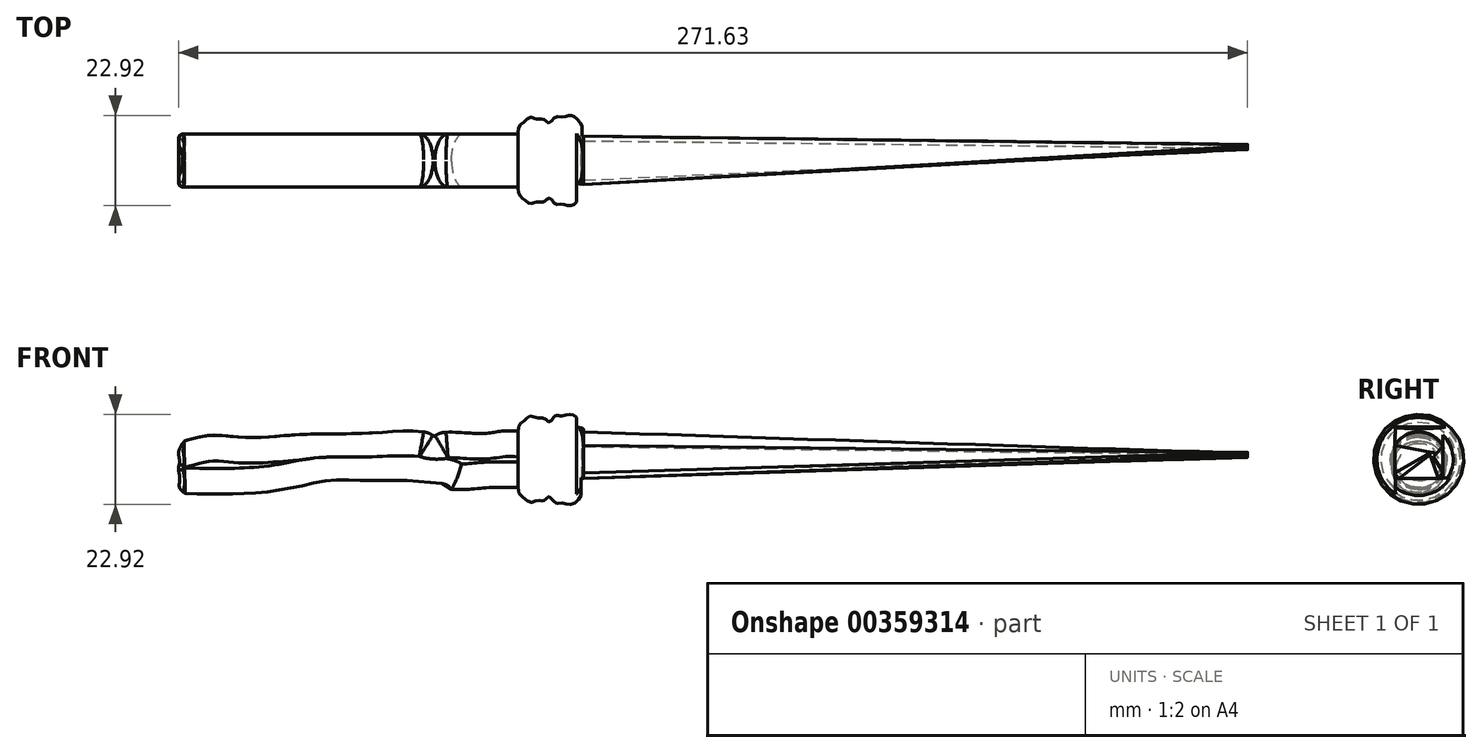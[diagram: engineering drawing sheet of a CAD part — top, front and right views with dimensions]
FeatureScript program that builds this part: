
annotation { "Feature Type Name" : "Feature", "Feature Type Description" : "" }
export const myFeature = defineFeature(function(context is Context, id is Id, definition is map)
    precondition{}
    {
        {
            var Q0;
            Q0=qCreatedBy(makeId("Front.planeOp"),FACE);
            var sketch = newSketch(context, id + "F0", { "sketchPlane" : qUnion([Q0])});
            skFitSpline(sketch, "E0", {"points": [v(-136.71, 3.5) * mm, v(-129.4, 4.98) * mm, v(-121.58, 4.4) * mm, v(-107.37, 5.13) * mm, v(-92.29, 5.42) * mm, v(-84.6, 5.85) * mm, v(-74.74, 5.56) * mm, v(-73.15, 4.84) * mm, v(-71.4, 5.56) * mm, v(-61.4, 5.42) * mm, v(-56.04, 6) * mm, v(-51.83, 6) * mm], "startDerivative": vector(88.1, 22.8) * mm, "endDerivative": vector(61.32, -2.92) * mm});
            skFitSpline(sketch, "E1", {"points": [v(-136.42, -9.83) * mm, v(-121.1, -9.83) * mm, v(-111.3, -8.78) * mm, v(-105.26, -7.5) * mm, v(-100.26, -6.52) * mm, v(-91.17, -6.52) * mm, v(-80.75, -6.52) * mm, v(-73.68, -7) * mm, v(-69.65, -7.8) * mm, v(-68.74, -8.78) * mm], "startDerivative": vector(97.79, -2) * mm, "endDerivative": vector(13.86, -22.1) * mm});
            skFitSpline(sketch, "E2", {"points": [v(-68.74, -8.78) * mm, v(-64.65, -8.78) * mm, v(-58.92, -8.29) * mm, v(-54.41, -8.29) * mm, v(-51.73, -8.29) * mm], "startDerivative": vector(15.61, -0.53) * mm, "endDerivative": vector(12, 0.12) * mm});
            skLineSegment(sketch, "E3", {"start": v(-51.83, 6) * mm, "end": v(-51.83, -8.29) * mm});
            skLineSegment(sketch, "E4", {"start": v(-136.71, 3.5) * mm, "end": v(-136.42, -9.83) * mm});
            skSolve(sketch);
        }
        {
            var Q0;
            Q0 = qSketchRegion(id + "F0", true);
            extrude(context, id + "F1", {"entities" : qUnion([Q0]), "endBound" : BoundingType.SYMMETRIC, "depth" : 13.5 * mm});
        }
        {
            var Q0;
            Q0=makeQuery(id+"F1.opExtrude","CAP_EDGE",EDGE,{"disambiguationData":[OSD([sQuery(id+"F0.wireOp",EDGE,"E0")])],"isStart":false});
            var Q1;
            Q1=makeQuery(id+"F1.opExtrude","CAP_EDGE",EDGE,{"disambiguationData":[OSD([sQuery(id+"F0.wireOp",EDGE,"E0")])],"isStart":true});
            var Q2;
            Q2=makeQuery(id+"F1.opExtrude","CAP_EDGE",EDGE,{"disambiguationData":[OSD([sQuery(id+"F0.wireOp",EDGE,"E1")])],"isStart":false});
            var Q3;
            Q3=makeQuery(id+"F1.opExtrude","CAP_EDGE",EDGE,{"disambiguationData":[OSD([sQuery(id+"F0.wireOp",EDGE,"E1")])],"isStart":true});
            var Q4;
            Q4=makeQuery(id+"F1.opExtrude","CAP_EDGE",EDGE,{"disambiguationData":[OSD([sQuery(id+"F0.wireOp",EDGE,"E2")])],"isStart":false});
            var Q5;
            Q5=makeQuery(id+"F1.opExtrude","CAP_EDGE",EDGE,{"disambiguationData":[OSD([sQuery(id+"F0.wireOp",EDGE,"E2")])],"isStart":true});
            fillet(context, id + "F2", {"entities" : qUnion([Q0, Q1, Q2, Q3, Q4, Q5]), "radius" : 6.5 * mm, "tangentPropagation" : true, "allowEdgeOverflow" : false});
        }
        {
            var Q0;
            Q0=qCreatedBy(makeId("Front.planeOp"),FACE);
            var sketch = newSketch(context, id + "F3", { "sketchPlane" : qUnion([Q0])});
            skFitSpline(sketch, "E5.0", {"points": [v(-136.57, -3.18) * mm, v(-136.58, -2.74) * mm, v(-136.59, -2.1) * mm, v(-136.6, -1.27) * mm, v(-136.63, -0.44) * mm, v(-136.65, 0.5) * mm, v(-136.67, 1.54) * mm, v(-136.69, 2.23) * mm, v(-136.7, 2.7) * mm, v(-136.7, 3.08) * mm, v(-136.71, 3.4) * mm, v(-136.71, 3.5) * mm, v(-136.71, 3.5) * mm]});
            skFitSpline(sketch, "E6.0", {"points": [v(-136.42, -9.83) * mm, v(-136.42, -9.83) * mm, v(-136.42, -9.77) * mm, v(-136.42, -9.56) * mm, v(-136.43, -9.27) * mm, v(-136.44, -8.77) * mm, v(-136.46, -8.09) * mm, v(-136.47, -7.46) * mm, v(-136.48, -6.95) * mm, v(-136.5, -6.4) * mm, v(-136.5, -5.82) * mm, v(-136.52, -5.22) * mm, v(-136.54, -4.4) * mm, v(-136.55, -3.75) * mm, v(-136.56, -3.32) * mm]});
            skFitSpline(sketch, "E7", {"points": [v(-136.42, -9.83) * mm, v(-137.89, -8.23) * mm, v(-137.76, -6.04) * mm, v(-138.13, -3.54) * mm, v(-137.83, -1.9) * mm, v(-138.07, 0) * mm, v(-137.89, 1.4) * mm, v(-136.71, 3.5) * mm], "startDerivative": vector(-13.14, 9.88) * mm, "endDerivative": vector(8.96, 14.17) * mm});
            skLineSegment(sketch, "E8", {"start": v(-136.57, -3.18) * mm, "end": v(-136.56, -3.32) * mm});
            skSolve(sketch);
        }
        {
            var Q0;
            Q0 = qSketchRegion(id + "F3", true);
            extrude(context, id + "F4", {"entities" : qUnion([Q0]), "endBound" : BoundingType.SYMMETRIC, "depth" : 13.5 * mm});
        }
        {
            var Q0;
            Q0=makeQuery(id+"F4.opExtrude","SWEPT_FACE",FACE,{"disambiguationData":[OSD([sQuery(id+"F3.wireOp",EDGE,"E5.0")])]});
            var sketch = newSketch(context, id + "F5", { "sketchPlane" : qUnion([Q0])});
            skFitSpline(sketch, "E9.0", {"points": [v(0.25, 6.56) * mm, v(0.69, 6.56) * mm, v(1.33, 6.5) * mm, v(2.16, 6.28) * mm, v(2.98, 5.97) * mm, v(3.72, 5.56) * mm, v(4.41, 5.03) * mm, v(4.88, 4.58) * mm, v(5.3, 4.1) * mm, v(5.68, 3.57) * mm, v(6, 3) * mm, v(6.27, 2.42) * mm, v(6.48, 1.8) * mm, v(6.69, 0.96) * mm, v(6.75, 0.32) * mm, v(6.75, -0.12) * mm]});
            skFitSpline(sketch, "E10.0", {"points": [v(-6.75, -0.12) * mm, v(-6.75, 0.32) * mm, v(-6.69, 0.96) * mm, v(-6.49, 1.8) * mm, v(-6.28, 2.42) * mm, v(-6, 3) * mm, v(-5.69, 3.56) * mm, v(-5.31, 4.09) * mm, v(-4.74, 4.74) * mm, v(-4.1, 5.3) * mm, v(-3.35, 5.76) * mm, v(-2.78, 6.05) * mm, v(-2.17, 6.27) * mm, v(-1.55, 6.44) * mm, v(-0.9, 6.54) * mm, v(-0.47, 6.56) * mm, v(-0.25, 6.56) * mm]});
            skFitSpline(sketch, "E11.0", {"points": [v(-0.25, -6.77) * mm, v(-0.68, -6.77) * mm, v(-1.31, -6.7) * mm, v(-2.14, -6.5) * mm, v(-2.95, -6.2) * mm, v(-3.7, -5.81) * mm, v(-4.38, -5.3) * mm, v(-4.85, -4.87) * mm, v(-5.28, -4.4) * mm, v(-5.66, -3.89) * mm, v(-6, -3.33) * mm, v(-6.26, -2.76) * mm, v(-6.48, -2.16) * mm, v(-6.69, -1.33) * mm, v(-6.75, -0.7) * mm, v(-6.75, -0.26) * mm]});
            skFitSpline(sketch, "E12.0", {"points": [v(6.75, -0.26) * mm, v(6.75, -0.7) * mm, v(6.69, -1.32) * mm, v(6.48, -2.15) * mm, v(6.2, -2.96) * mm, v(5.8, -3.7) * mm, v(5.29, -4.4) * mm, v(4.86, -4.87) * mm, v(4.39, -5.3) * mm, v(3.87, -5.68) * mm, v(3.32, -6) * mm, v(2.75, -6.28) * mm, v(2.15, -6.5) * mm, v(1.53, -6.65) * mm, v(0.9, -6.75) * mm, v(0.46, -6.77) * mm, v(0.25, -6.77) * mm]});
            skLineSegment(sketch, "E13.bottom", {"start": v(7.5, 6.97) * mm, "end": v(-7.45, 6.97) * mm});
            skLineSegment(sketch, "E13.top", {"start": v(7.5, -7.56) * mm, "end": v(-7.45, -7.56) * mm});
            skLineSegment(sketch, "E13.left", {"start": v(7.5, 6.97) * mm, "end": v(7.5, -7.56) * mm});
            skLineSegment(sketch, "E13.right", {"start": v(-7.45, 6.97) * mm, "end": v(-7.45, -7.56) * mm});
            skLineSegment(sketch, "E14", {"start": v(6.75, -0.12) * mm, "end": v(6.75, -0.26) * mm});
            skLineSegment(sketch, "E15", {"start": v(0.25, 6.56) * mm, "end": v(-0.25, 6.56) * mm});
            skLineSegment(sketch, "E16", {"start": v(-6.75, -0.12) * mm, "end": v(-6.75, -0.26) * mm});
            skLineSegment(sketch, "E17", {"start": v(0.25, -6.77) * mm, "end": v(-0.25, -6.77) * mm});
            skSolve(sketch);
        }
        {
            var Q0;
            Q0 = qSketchRegion(id + "F5", true);
            extrude(context, id + "F6", {"entities" : qUnion([Q0]), "operationType" : NewBodyOperationType.REMOVE, "oppositeDirection" : true, "depth" : 25 * mm});
        }
        {
            var Q0;
            Q0=makeQuery(id+"F6.boolean.opBoolean","INTERSECT",EDGE,{"derivedFrom":[makeQuery(id+"F4.opExtrude","SWEPT_FACE",FACE,{"disambiguationData":[OSD([sQuery(id+"F3.wireOp",EDGE,"E7")])]}),makeQuery(id+"F6.opExtrude","SWEPT_FACE",FACE,{"disambiguationData":[OSD([sQuery(id+"F5.wireOp",EDGE,"E9.0")])]})]});
            var Q1;
            Q1=makeQuery(id+"F6.boolean.opBoolean","INTERSECT",EDGE,{"derivedFrom":[makeQuery(id+"F4.opExtrude","SWEPT_FACE",FACE,{"disambiguationData":[OSD([sQuery(id+"F3.wireOp",EDGE,"E7")])]}),makeQuery(id+"F6.opExtrude","SWEPT_FACE",FACE,{"disambiguationData":[OSD([sQuery(id+"F5.wireOp",EDGE,"E10.0")])]})]});
            var Q2;
            Q2=makeQuery(id+"F6.boolean.opBoolean","INTERSECT",EDGE,{"derivedFrom":[makeQuery(id+"F4.opExtrude","SWEPT_FACE",FACE,{"disambiguationData":[OSD([sQuery(id+"F3.wireOp",EDGE,"E7")])]}),makeQuery(id+"F6.opExtrude","SWEPT_FACE",FACE,{"disambiguationData":[OSD([sQuery(id+"F5.wireOp",EDGE,"E11.0")])]})]});
            var Q3;
            Q3=makeQuery(id+"F6.boolean.opBoolean","INTERSECT",EDGE,{"derivedFrom":[makeQuery(id+"F4.opExtrude","SWEPT_FACE",FACE,{"disambiguationData":[OSD([sQuery(id+"F3.wireOp",EDGE,"E7")])]}),makeQuery(id+"F6.opExtrude","SWEPT_FACE",FACE,{"disambiguationData":[OSD([sQuery(id+"F5.wireOp",EDGE,"E12.0")])]})]});
            fillet(context, id + "F7", {"entities" : qUnion([Q0, Q1, Q2, Q3]), "radius" : 1.2 * mm, "tangentPropagation" : true, "allowEdgeOverflow" : false});
        }
        {
            var Q0;
            Q0=qCreatedBy(makeId("Front.planeOp"),FACE);
            var sketch = newSketch(context, id + "F8", { "sketchPlane" : qUnion([Q0])});
            skFitSpline(sketch, "E18", {"points": [v(-35.19, 5.8) * mm, v(-35.43, 7.21) * mm, v(-36.25, 8.66) * mm, v(-37.93, 10.17) * mm, v(-39.27, 10.22) * mm, v(-40.89, 9.91) * mm, v(-42.25, 9.95) * mm, v(-43.48, 8.66) * mm, v(-44.13, 8.4) * mm, v(-45.19, 9.24) * mm, v(-47.28, 9.38) * mm, v(-48.68, 9.86) * mm, v(-50.1, 8.87) * mm, v(-51.5, 7.6) * mm, v(-51.9, 5.99) * mm], "startDerivative": vector(-2.17, 21.09) * mm, "endDerivative": vector(-3.04, -22.68) * mm});
            skLineSegment(sketch, "E19", {"start": v(-51.9, 5.99) * mm, "end": v(-51.9, 0) * mm});
            skLineSegment(sketch, "E20", {"start": v(-51.9, -1.15) * mm, "end": v(-33.41, -1.15) * mm});
            skLineSegment(sketch, "E21", {"start": v(-51.9, 5.99) * mm, "end": v(-51.9, -1.15) * mm});
            skLineSegment(sketch, "E22", {"start": v(-35.19, 5.8) * mm, "end": v(-35.19, -1.15) * mm});
            skSolve(sketch);
        }
        {
            var Q0;
            Q0 = qSketchRegion(id + "F8", true);
            var Q1;
            Q1=sQuery(id+"F8.wireOp",EDGE,"E20");
            revolve(context, id + "F9", {"operationType" : NewBodyOperationType.ADD, "entities" : qUnion([Q0]), "axis" : qUnion([Q1]), "revolveType" : RevolveType.FULL});
        }
        {
            var Q0;
            Q0=qCreatedBy(makeId("Front.planeOp"),FACE);
            var sketch = newSketch(context, id + "F10", { "sketchPlane" : qUnion([Q0])});
            skFitSpline(sketch, "E23", {"points": [v(-35.35, 5.83) * mm, v(-30.73, 6.04) * mm, v(-26.22, 5.12) * mm, v(-22.74, 5.42) * mm, v(-15.05, 5.42) * mm, v(-7.25, 4.91) * mm, v(-1.72, 4.5) * mm, v(2.7, 5.32) * mm, v(8.13, 5.63) * mm, v(13.36, 5.12) * mm, v(19.4, 5.94) * mm, v(24.53, 5.83) * mm, v(29.45, 5.32) * mm, v(41.24, 6.24) * mm, v(48.73, 7.58) * mm, v(55.8, 8.7) * mm, v(62.06, 10.24) * mm, v(67.6, 10.24) * mm, v(77.23, 10.14) * mm, v(85.54, 9.63) * mm, v(91.38, 9.22) * mm, v(97.53, 8.4) * mm, v(104.81, 7.47) * mm, v(112.2, 7.17) * mm, v(121.32, 5.73) * mm, v(127.88, 4.7) * mm, v(130.86, 4.7) * mm, v(133.22, 3.89) * mm, v(133.93, 2.35) * mm, v(129.11, 1.83) * mm, v(120.1, 2.14) * mm, v(109.43, 2.76) * mm, v(93.43, 3.37) * mm, v(84, 3.78) * mm, v(76.72, 3.17) * mm, v(68, 2.66) * mm, v(64.1, 1.94) * mm, v(55.19, 0) * mm, v(48.42, -1.45) * mm, v(39.3, -2.88) * mm, v(29.97, -4.83) * mm, v(21.66, -4.83) * mm, v(15.3, -5.96) * mm, v(3.92, -6.06) * mm, v(-6.33, -6.37) * mm, v(-14.64, -6.06) * mm, v(-19.86, -7.5) * mm, v(-29.1, -7.3) * mm, v(-32.93, -6.99) * mm, v(-36.45, -7.69) * mm], "startDerivative": vector(270.47, 36.12) * mm, "endDerivative": vector(-243.68, -50.6) * mm});
            skLineSegment(sketch, "E24", {"start": v(-35.35, 5.83) * mm, "end": v(-35.35, -7.44) * mm});
            skSolve(sketch);
        }
        {
            var Q0;
            Q0 = qSketchRegion(id + "F10", true);
            extrude(context, id + "F11", {"entities" : qUnion([Q0]), "endBound" : BoundingType.SYMMETRIC, "depth" : 19.8 * mm});
        }
        {
            var Q0;
            Q0=qCreatedBy(makeId("Top.planeOp"),FACE);
            var sketch = newSketch(context, id + "F12", { "sketchPlane" : qUnion([Q0])});
            skFitSpline(sketch, "E25", {"points": [v(-35.6, 6.18) * mm, v(-29.65, 5.77) * mm, v(-23.5, 4.85) * mm, v(-14.57, 5.67) * mm, v(-6.06, 4.75) * mm, v(4.19, 5.05) * mm, v(13.83, 5.87) * mm, v(23.36, 5.87) * mm, v(30.64, 5.26) * mm, v(39.56, 6.08) * mm, v(48.9, 7.51) * mm, v(59.7, 8.62) * mm, v(75.58, 9.7) * mm, v(90.73, 9.05) * mm, v(99.5, 7.9) * mm, v(111.64, 6.6) * mm, v(126, 4.54) * mm, v(132.76, 4.13) * mm, v(133.84, 3.2) * mm, v(131.12, 1.98) * mm, v(119.54, 1.88) * mm, v(108.77, 3) * mm, v(96.47, 3.41) * mm, v(84.93, 4.2) * mm, v(66.22, 2.9) * mm, v(57.6, 0) * mm, v(40.7, -2.84) * mm, v(30.03, -4.69) * mm, v(24.5, -4.79) * mm, v(19.47, -4.69) * mm, v(9.73, -5.92) * mm, v(-2.88, -5.5) * mm, v(-13.96, -6.22) * mm, v(-18.16, -7.35) * mm, v(-28.42, -6.84) * mm, v(-36.93, -5.81) * mm], "startDerivative": vector(264.56, -6.57) * mm, "endDerivative": vector(-291.2, 36.39) * mm});
            skLineSegment(sketch, "E26", {"start": v(-35.6, 6.18) * mm, "end": v(-35.6, 14.97) * mm});
            skLineSegment(sketch, "E27", {"start": v(-35.6, 14.97) * mm, "end": v(137.98, 14.97) * mm});
            skLineSegment(sketch, "E28", {"start": v(137.98, 14.97) * mm, "end": v(137.98, -15.03) * mm});
            skLineSegment(sketch, "E29", {"start": v(137.98, -15.03) * mm, "end": v(-36.93, -15.03) * mm});
            skLineSegment(sketch, "E30", {"start": v(-36.93, -15.03) * mm, "end": v(-36.93, -5.81) * mm});
            skSolve(sketch);
        }
        {
            var Q0;
            Q0 = qSketchRegion(id + "F12", true);
            extrude(context, id + "F13", {"entities" : qUnion([Q0]), "operationType" : NewBodyOperationType.REMOVE, "endBound" : BoundingType.SYMMETRIC, "oppositeDirection" : true, "depth" : 36 * mm});
        }
        {
            var Q0;
            Q0=makeQuery(id+"F11.opExtrude","SWEPT_BODY",BODY,{"disambiguationData":[OSD([sQuery(id+"F10.wireOp",EDGE,"E23"),sQuery(id+"F10.wireOp",EDGE,"E24")])]});
            deleteBodies(context, id + "F14", {"entities" : qUnion([Q0])});
        }
        {
            var Q0;
            Q0=qCreatedBy(makeId("Top.planeOp"),FACE);
            var sketch = newSketch(context, id + "F15", { "sketchPlane" : qUnion([Q0])});
            skFitSpline(sketch, "E31", {"points": [v(-36.22, 6.67) * mm, v(-30.38, 6.3) * mm, v(-27.01, 5.75) * mm, v(-22.82, 5.21) * mm, v(-12.4, 5.43) * mm, v(-6.42, 4.78) * mm, v(-2.02, 4.64) * mm, v(2.74, 5.5) * mm, v(9.37, 5.65) * mm, v(15.13, 5.29) * mm, v(21.62, 6.08) * mm, v(28.4, 5.65) * mm, v(38.63, 5.65) * mm, v(45.19, 7.38) * mm, v(54.05, 8.67) * mm, v(60.97, 10.33) * mm, v(71.2, 10.19) * mm, v(80.93, 10.26) * mm, v(88.57, 9.4) * mm, v(98.23, 8.67) * mm, v(104.21, 7.52) * mm, v(110.91, 7.3) * mm, v(114.59, 6.87) * mm, v(120.43, 5.65) * mm, v(125.76, 5) * mm, v(130.95, 5) * mm, v(133.54, 4.2) * mm, v(133.69, 2.83) * mm, v(130.23, 1.97) * mm, v(113.87, 2.7) * mm, v(94.12, 3.41) * mm, v(85.04, 3.84) * mm, v(77.83, 3.12) * mm, v(70.77, 2.76) * mm, v(65.36, 2.33) * mm, v(58.37, 0.82) * mm, v(49.08, -1.35) * mm, v(32.36, -4.23) * mm, v(27.24, -5.1) * mm, v(22.84, -4.59) * mm, v(16.65, -5.89) * mm, v(7.35, -6.17) * mm, v(-3.53, -5.89) * mm, v(-10.02, -6.4) * mm, v(-15.35, -6.53) * mm, v(-19.9, -7.47) * mm, v(-28.54, -7.18) * mm, v(-36.1, -6.6) * mm], "startDerivative": vector(302.49, 22.06) * mm, "endDerivative": vector(-324.86, 23.14) * mm});
            skLineSegment(sketch, "E32", {"start": v(-35.61, -7.13) * mm, "end": v(-35.61, 6.58) * mm});
            skLineSegment(sketch, "E33", {"start": v(-35.61, 6.58) * mm, "end": v(-35.61, 6.96) * mm});
            skSolve(sketch);
        }
        {
            var Q0;
            Q0 = qSketchRegion(id + "F15", true);
            extrude(context, id + "F16", {"entities" : qUnion([Q0]), "endBound" : BoundingType.SYMMETRIC, "depth" : 25 * mm});
        }
        {
            var Q0;
            Q0=qCreatedBy(makeId("Front.planeOp"),FACE);
            var sketch = newSketch(context, id + "F17", { "sketchPlane" : qUnion([Q0])});
            skFitSpline(sketch, "E34", {"points": [v(-35.8, -5.9) * mm, v(-32.73, -6.43) * mm, v(-27.86, -7.27) * mm, v(-22.4, -7.37) * mm, v(-18.97, -7.44) * mm, v(-15.23, -6.57) * mm, v(-12.02, -6.43) * mm, v(-3.77, -6.18) * mm, v(8.67, -6.04) * mm, v(14.5, -6.12) * mm, v(21.61, -5) * mm, v(27.7, -5.1) * mm, v(38.33, -3.04) * mm, v(46.38, -1.75) * mm, v(56.17, 0.67) * mm, v(59.38, 0.77) * mm, v(64.99, 2.45) * mm, v(70.24, 2.8) * mm, v(80.83, 3.52) * mm, v(87.36, 4.03) * mm, v(100.7, 3.22) * mm, v(113.76, 2.8) * mm, v(121.9, 2.1) * mm, v(130.06, 2.2) * mm, v(132.6, 2.26) * mm, v(133.63, 3.17) * mm, v(132.45, 4.23) * mm, v(129.78, 4.83) * mm, v(124.4, 5.01) * mm, v(116.9, 6.35) * mm, v(112.64, 7.07) * mm, v(105.94, 7.21) * mm, v(94.98, 8.73) * mm, v(89.15, 9.67) * mm, v(82.44, 10.24) * mm, v(74.66, 9.88) * mm, v(68.32, 9.95) * mm, v(61.26, 10.1) * mm, v(56.36, 8.87) * mm, v(48.64, 7.94) * mm, v(40.57, 6.06) * mm, v(28.18, 5.41) * mm, v(21.9, 6.13) * mm, v(13.4, 5.27) * mm, v(3.46, 5.49) * mm, v(-2.96, 4.62) * mm, v(-9.95, 5.12) * mm, v(-21.26, 5.2) * mm, v(-29.62, 5.7) * mm, v(-37.05, 7.07) * mm], "startDerivative": vector(209.33, -32.96) * mm, "endDerivative": vector(-341.15, 71.6) * mm});
            skLineSegment(sketch, "E35", {"start": v(-37.05, 7.07) * mm, "end": v(-37.05, 15.46) * mm});
            skLineSegment(sketch, "E36", {"start": v(-37.05, 15.46) * mm, "end": v(137.26, 15.46) * mm});
            skLineSegment(sketch, "E37", {"start": v(137.26, 15.46) * mm, "end": v(137.26, -17.52) * mm});
            skLineSegment(sketch, "E38", {"start": v(137.26, -17.52) * mm, "end": v(-35.8, -17.52) * mm});
            skLineSegment(sketch, "E39", {"start": v(-35.8, -17.52) * mm, "end": v(-35.8, -5.9) * mm});
            skSolve(sketch);
        }
        {
            var Q0;
            Q0 = qSketchRegion(id + "F17", true);
            extrude(context, id + "F18", {"entities" : qUnion([Q0]), "operationType" : NewBodyOperationType.REMOVE, "endBound" : BoundingType.SYMMETRIC, "depth" : 25 * mm});
        }
        {
            var Q0;
            Q0=makeQuery(id+"F18.boolean.opBoolean","INTERSECT",EDGE,{"disambiguationData":[OD(1.0)],"derivedFrom":[makeQuery(id+"F16.opExtrude","SWEPT_FACE",FACE,{"disambiguationData":[OSD([sQuery(id+"F15.wireOp",EDGE,"E31")])]}),makeQuery(id+"F18.opExtrude","SWEPT_FACE",FACE,{"disambiguationData":[OSD([sQuery(id+"F17.wireOp",EDGE,"E34")])]})]});
            var Q1;
            Q1=makeQuery(id+"F18.boolean.opBoolean","INTERSECT",EDGE,{"disambiguationData":[OD(0.0)],"derivedFrom":[makeQuery(id+"F16.opExtrude","SWEPT_FACE",FACE,{"disambiguationData":[OSD([sQuery(id+"F15.wireOp",EDGE,"E31")])]}),makeQuery(id+"F18.opExtrude","SWEPT_FACE",FACE,{"disambiguationData":[OSD([sQuery(id+"F17.wireOp",EDGE,"E34")])]})]});
            fillet(context, id + "F19", {"entities" : qUnion([Q0, Q1]), "radius" : 1 * mm, "tangentPropagation" : true, "allowEdgeOverflow" : false});
        }
        {
            var Q0;
            Q0=qCreatedBy(makeId("Top.planeOp"),FACE);
            var sketch = newSketch(context, id + "F20", { "sketchPlane" : qUnion([Q0])});
            skFitSpline(sketch, "E40", {"points": [v(-35.6, -0.64) * mm, v(-31.93, -0.88) * mm, v(-26.57, -1.1) * mm, v(-16.66, -1) * mm, v(-3.78, -0.38) * mm, v(7.22, 0) * mm, v(31.33, 0.7) * mm, v(41.14, 1.79) * mm, v(55.05, 4.74) * mm, v(63.07, 6.45) * mm, v(74.59, 6.98) * mm, v(85.41, 6.65) * mm, v(95.28, 6.04) * mm, v(109.95, 5) * mm, v(118.72, 3.98) * mm, v(127.7, 3.43) * mm, v(133.6, 3.43) * mm], "startDerivative": vector(94.88, -6.49) * mm, "endDerivative": vector(115.97, 1.65) * mm});
            skSolve(sketch);
        }
        {
            var Q0;
            Q0=makeQuery(id+"F9.opRevolve","SWEPT_FACE",FACE,{"disambiguationData":[OSD([sQuery(id+"F8.wireOp",EDGE,"E22")])]});
            var sketch = newSketch(context, id + "F21", { "sketchPlane" : qUnion([Q0])});
            skCircle(sketch, "E41.0.0", {"center": v(0, -1.15) * mm, "radius": 6.96 * mm});
            skSolve(sketch);
        }
        {
            var Q0;
            Q0=qCreatedBy(makeId("Right.planeOp"),FACE);
            cPlane(context, id + "F22", {"entities" : qUnion([Q0]), "cplaneType" : CPlaneType.OFFSET, "offset" : 133.5 * mm, "width" : 150 * mm, "height" : 150 * mm});
        }
        {
            var Q0;
            Q0=qCreatedBy(id+"F22.planeOp",FACE);
            var sketch = newSketch(context, id + "F23", { "sketchPlane" : qUnion([Q0])});
            skPoint(sketch, "E42.0", {"position": v(3.43, 0) * mm});
            skCircle(sketch, "E43", {"center": v(3.43, 0) * mm, "radius": 0.65 * mm});
            skSolve(sketch);
        }
        {
            var Q0;
            Q0=makeQuery(id+"F21.imprint","IMPRINT",FACE,{"disambiguationData":[TD([[makeQuery(id+"F21.imprint","IMPRINT",EDGE,{"derivedFrom":sQuery(id+"F21.wireOp",EDGE,"E41.0.0")}),-1.0]])]});
            var Q1;
            Q1=makeQuery(id+"F23.imprint","IMPRINT",FACE,{"disambiguationData":[TD([[makeQuery(id+"F23.imprint","IMPRINT",EDGE,{"derivedFrom":sQuery(id+"F23.wireOp",EDGE,"E43")}),1.0]])]});
            var Q2;
            Q2=sQuery(id+"F20.wireOp",EDGE,"E40");
            loft(context, id + "F24", {"sheetProfilesArray" : [{ "sheetProfileEntities" : qUnion([Q0]) }, { "sheetProfileEntities" : qUnion([Q1]) }], "guidesArray" : [{ "guideEntities" : qUnion([Q2]), "guideDerivativeType" : LoftGuideDerivativeType.DEFAULT, "guideDerivativeMagnitude" : 1 }]});
        }
        {
            var Q0;
            Q0=makeQuery(id+"F16.opExtrude","SWEPT_BODY",BODY,{"disambiguationData":[OSD([sQuery(id+"F15.wireOp",EDGE,"E31"),sQuery(id+"F15.wireOp",EDGE,"E32"),sQuery(id+"F15.wireOp",EDGE,"E33")])]});
            deleteBodies(context, id + "F25", {"entities" : qUnion([Q0])});
        }
    });
